# Revit family: Magnuson-Madison-Screen_Acoustic-1
name_source: partatom
category: Furniture
revit_build: Autodesk Revit 2014 (Build: 20130308_1515(x64)
units: mm (PartAtom-declared; Revit-internal decimal feet)

## types (1)
- Type Catalog
    Assembly Code = E2020200
    Base v1 = Yes
    Base v2 = No
    Cost = 0 $
    Depth = 200 mm
    Description = Desktop screen with acoustic fabric and one circular base on the side
    Dist Base = 580 mm  [stored 1.90289 ft]
    Height = 417.435 mm
    Keynote = 12500
    Manufacturer = Magnuson Group
    Model = MA-42-66-S
    Panel Back Finish = MAG - Fabric Ultramarine
    Panel Front Finish = MAG - Fabric Ultramarine
    Support Finish = MAG - Metal Black
    Type Comments = Madison
    URL = www.magnusongroup.com
    Width = 660 mm

note: [stored X ft] marks values corroborated as IEEE doubles in the binary element streams (Revit-internal decimal feet)

## geometry (parser evidence)
native form markers: Sweep x2
no freeform markers — native parametric forms only
